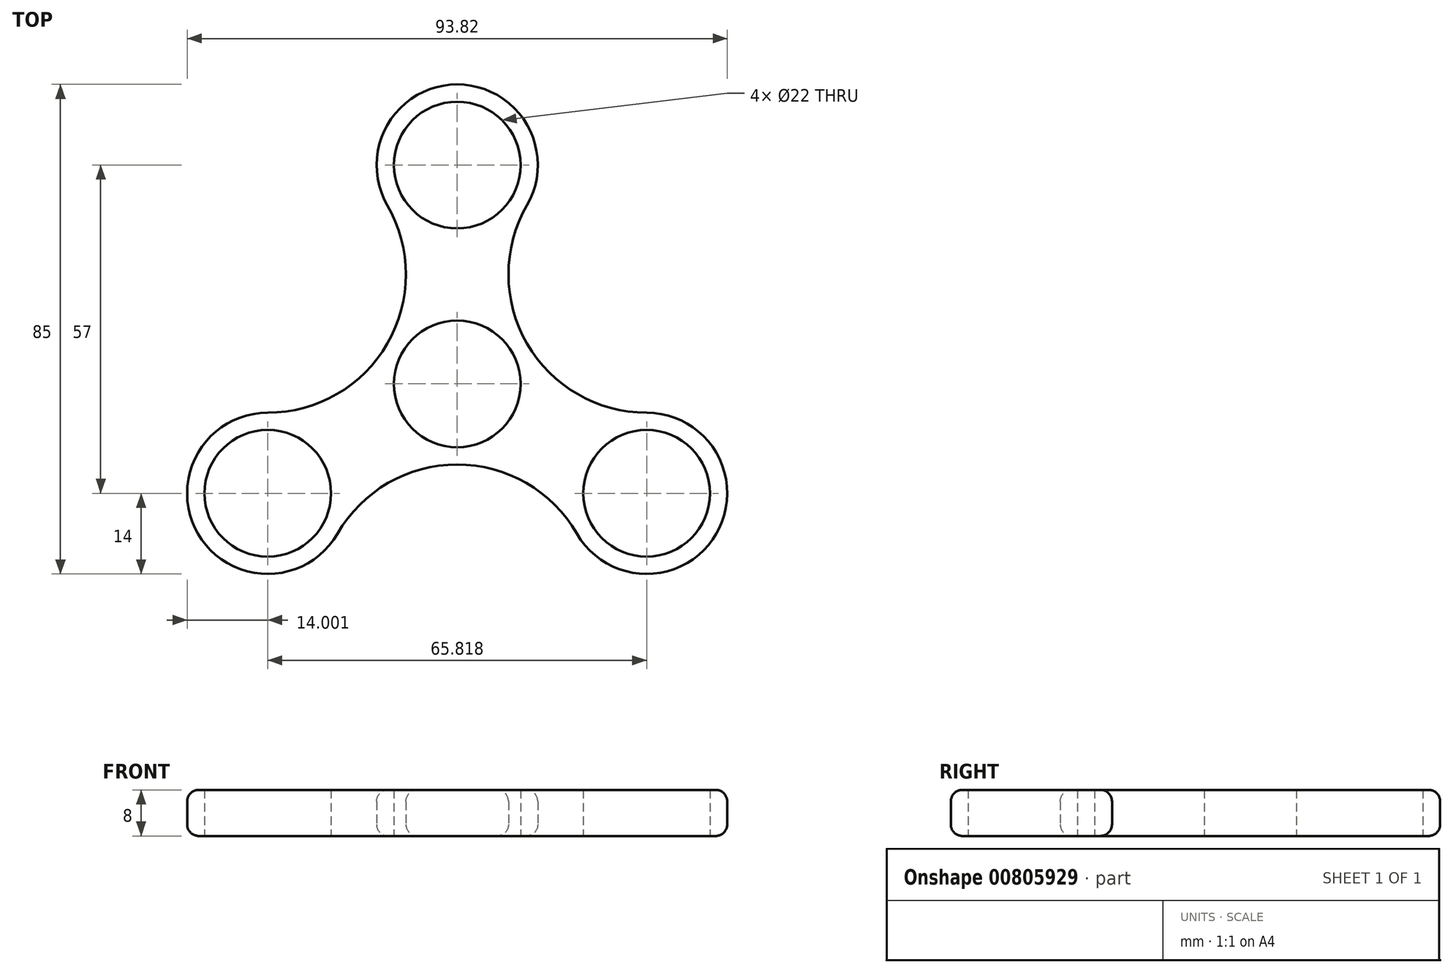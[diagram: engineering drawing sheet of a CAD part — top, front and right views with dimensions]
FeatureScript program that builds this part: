
annotation { "Feature Type Name" : "Feature", "Feature Type Description" : "" }
export const myFeature = defineFeature(function(context is Context, id is Id, definition is map)
    precondition{}
    {
        {
            var Q0;
            Q0=qCreatedBy(makeId("Top.planeOp"),FACE);
            var sketch = newSketch(context, id + "F0", { "sketchPlane" : qUnion([Q0])});
            skCircle(sketch, "E0", {"center": v(0, 0) * mm, "radius": 11 * mm});
            skCircle(sketch, "E1", {"center": v(0, 38) * mm, "radius": 11 * mm});
            skCircle(sketch, "E2.1.0", {"center": v(32.9, -19) * mm, "radius": 11 * mm});
            skCircle(sketch, "E2.2.0", {"center": v(-32.9, -19) * mm, "radius": 11 * mm});
            skCircle(sketch, "E3.0", {"center": v(-32.9, -19) * mm, "radius": 14 * mm});
            skCircle(sketch, "E4.0", {"center": v(0, 38) * mm, "radius": 14 * mm});
            skCircle(sketch, "E5.0", {"center": v(32.9, -19) * mm, "radius": 14 * mm});
            skCircle(sketch, "E6.0", {"center": v(0, 0) * mm, "radius": 14 * mm});
            skArc(sketch, "E7", {"start": v(20.78, -26) * mm, "mid": v(0, -14) * mm, "end": v(-20.78, -26) * mm});
            skArc(sketch, "E8.1.1", {"start": v(12.12, 31) * mm, "mid": v(12.12, 7) * mm, "end": v(32.9, -5) * mm});
            skArc(sketch, "E8.2.1", {"start": v(-32.9, -5) * mm, "mid": v(-12.12, 7) * mm, "end": v(-12.12, 31) * mm});
            skSolve(sketch);
        }
        {
            var Q0;
            {var subQ0=sQuery(id+"F0.wireOp",EDGE,"E8.1.1");var subQ1=sQuery(id+"F0.wireOp",EDGE,"E4.0");var subQ2=makeQuery(id+"F0.imprint","INTERSECT",VERTEX,{"derivedFrom":[subQ1,subQ0]});Q0=makeQuery(id+"F0.imprint","IMPRINT",FACE,{"disambiguationData":[TD([[makeQuery(id+"F0.imprint","IMPRINT",EDGE,{"disambiguationData":[TD([[subQ2,1.0]])],"derivedFrom":subQ1}),-1.0]])]});}
            var Q1;
            {var subQ0=sQuery(id+"F0.wireOp",EDGE,"E7");var subQ1=sQuery(id+"F0.wireOp",EDGE,"E5.0");var subQ2=makeQuery(id+"F0.imprint","INTERSECT",VERTEX,{"derivedFrom":[subQ1,subQ0]});Q1=makeQuery(id+"F0.imprint","IMPRINT",FACE,{"disambiguationData":[TD([[makeQuery(id+"F0.imprint","IMPRINT",EDGE,{"disambiguationData":[TD([[subQ2,1.0]])],"derivedFrom":subQ1}),-1.0]])]});}
            var Q2;
            Q2=makeQuery(id+"F0.imprint","IMPRINT",FACE,{"disambiguationData":[TD([[makeQuery(id+"F0.imprint","IMPRINT",EDGE,{"derivedFrom":sQuery(id+"F0.wireOp",EDGE,"E2.1.0")}),-1.0]])]});
            var Q3;
            Q3=makeQuery(id+"F0.imprint","IMPRINT",FACE,{"disambiguationData":[TD([[makeQuery(id+"F0.imprint","IMPRINT",EDGE,{"derivedFrom":sQuery(id+"F0.wireOp",EDGE,"E1")}),-1.0]])]});
            var Q4;
            {var subQ0=sQuery(id+"F0.wireOp",EDGE,"E7");var subQ1=sQuery(id+"F0.wireOp",EDGE,"E3.0");var subQ2=makeQuery(id+"F0.imprint","INTERSECT",VERTEX,{"derivedFrom":[subQ1,subQ0]});Q4=makeQuery(id+"F0.imprint","IMPRINT",FACE,{"disambiguationData":[TD([[makeQuery(id+"F0.imprint","IMPRINT",EDGE,{"disambiguationData":[TD([[subQ2,-1.0]])],"derivedFrom":subQ1}),-1.0]])]});}
            var Q5;
            Q5=makeQuery(id+"F0.imprint","IMPRINT",FACE,{"disambiguationData":[TD([[makeQuery(id+"F0.imprint","IMPRINT",EDGE,{"derivedFrom":sQuery(id+"F0.wireOp",EDGE,"E2.2.0")}),-1.0]])]});
            var Q6;
            Q6=makeQuery(id+"F0.imprint","IMPRINT",FACE,{"disambiguationData":[TD([[makeQuery(id+"F0.imprint","IMPRINT",EDGE,{"derivedFrom":sQuery(id+"F0.wireOp",EDGE,"E0")}),-1.0]])]});
            extrude(context, id + "F1", {"entities" : qUnion([Q0, Q1, Q2, Q3, Q4, Q5, Q6]), "depth" : 8 * mm, "offsetDistance" : 25 * mm});
        }
        {
            var Q0;
            Q0=makeQuery(id+"F1.opExtrude","CAP_EDGE",EDGE,{"disambiguationData":[OSD([sQuery(id+"F0.wireOp",EDGE,"E8.2.1")])],"isStart":false});
            var Q1;
            Q1=makeQuery(id+"F1.opExtrude","CAP_EDGE",EDGE,{"disambiguationData":[OSD([sQuery(id+"F0.wireOp",EDGE,"E8.2.1")])],"isStart":true});
            var Q2;
            Q2=makeQuery(id+"F1.opExtrude","CAP_EDGE",EDGE,{"disambiguationData":[OSD([sQuery(id+"F0.wireOp",EDGE,"E8.1.1")])],"isStart":true});
            var Q3;
            Q3=makeQuery(id+"F1.opExtrude","CAP_EDGE",EDGE,{"disambiguationData":[OSD([sQuery(id+"F0.wireOp",EDGE,"E4.0")])],"isStart":true});
            fillet(context, id + "F2", {"entities" : qUnion([Q0, Q1, Q2, Q3]), "radius" : 2 * mm, "tangentPropagation" : true, "allowEdgeOverflow" : false});
        }
    });
